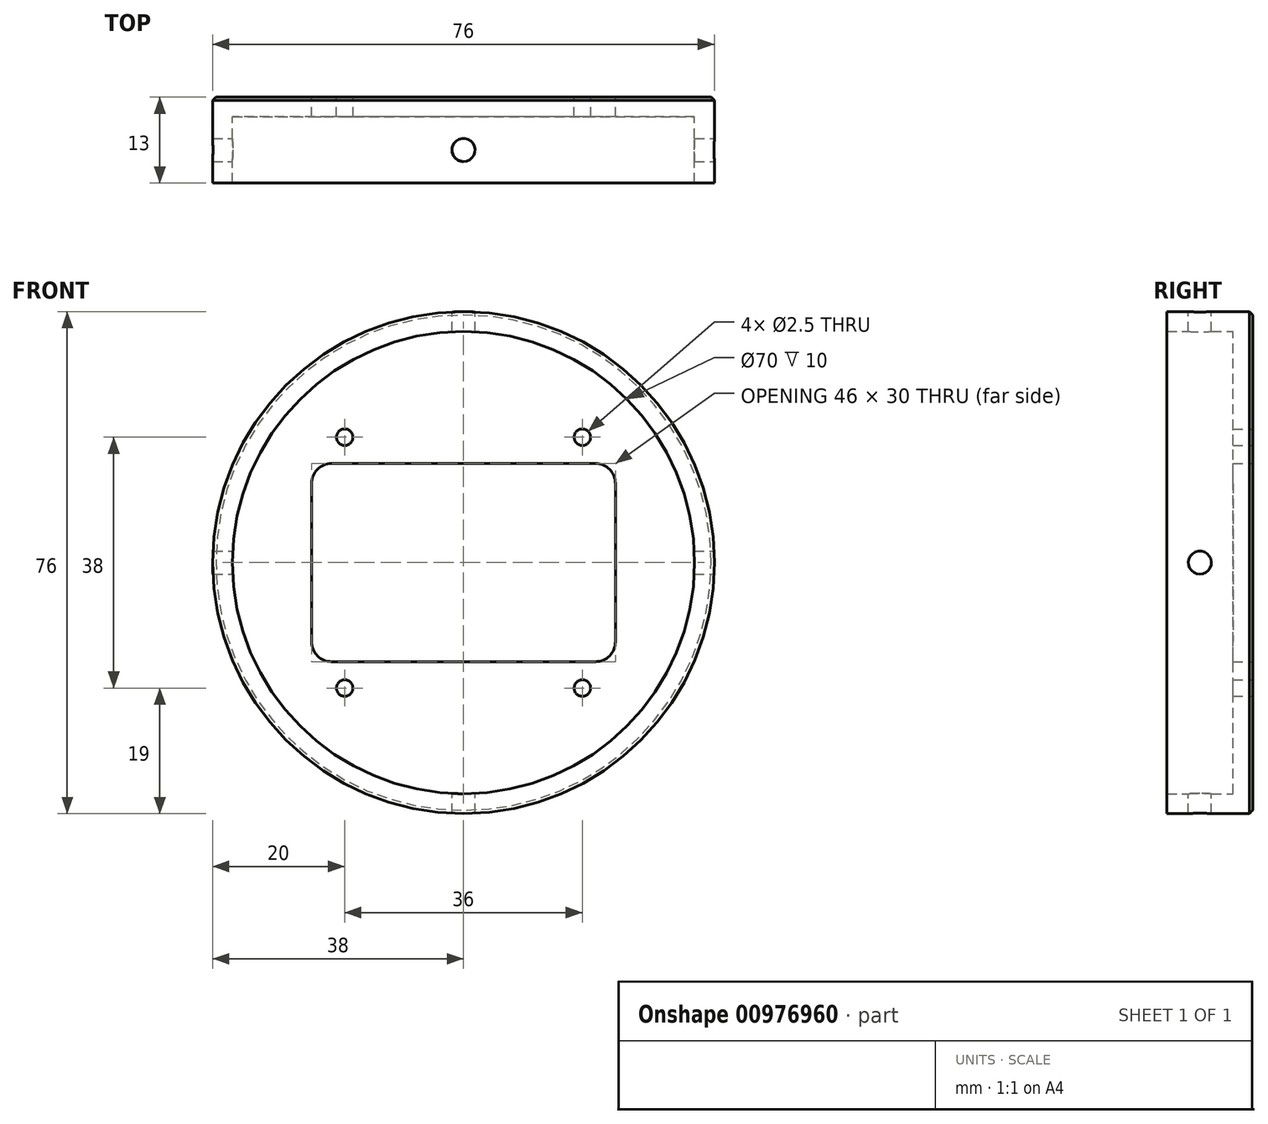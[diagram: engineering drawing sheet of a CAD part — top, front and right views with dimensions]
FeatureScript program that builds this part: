
annotation { "Feature Type Name" : "Feature", "Feature Type Description" : "" }
export const myFeature = defineFeature(function(context is Context, id is Id, definition is map)
    precondition{}
    {
        {
            var Q0;
            Q0=qCreatedBy(makeId("Front.planeOp"),FACE);
            var sketch = newSketch(context, id + "F0", { "sketchPlane" : qUnion([Q0])});
            skCircle(sketch, "E0", {"center": v(0, 0) * mm, "radius": 38 * mm});
            skSolve(sketch);
        }
        {
            var Q0;
            Q0=makeQuery(id+"F0.imprint","IMPRINT",FACE,{"disambiguationData":[TD([[makeQuery(id+"F0.imprint","IMPRINT",EDGE,{"derivedFrom":sQuery(id+"F0.wireOp",EDGE,"E0")}),1.0]])]});
            extrude(context, id + "F1", {"entities" : qUnion([Q0]), "depth" : 13 * mm, "offsetDistance" : 25 * mm});
        }
        {
            var Q0;
            Q0=makeQuery(id+"F1.opExtrude","CAP_FACE",FACE,{"disambiguationData":[OSD([sQuery(id+"F0.wireOp",EDGE,"E0")])],"isStart":false});
            shell(context, id + "F2", {"entities" : qUnion([Q0]), "thickness" : 3 * mm});
        }
        {
            var Q0;
            Q0=makeQuery(id+"F1.opExtrude","CAP_FACE",FACE,{"disambiguationData":[OSD([sQuery(id+"F0.wireOp",EDGE,"E0")])],"isStart":true});
            var sketch = newSketch(context, id + "F3", { "sketchPlane" : qUnion([Q0])});
            skPoint(sketch, "E1", {"position": v(-20, 12) * mm});
            skPoint(sketch, "E2", {"position": v(-20, -12) * mm});
            skPoint(sketch, "E3", {"position": v(20, -12) * mm});
            skPoint(sketch, "E4", {"position": v(20, 12) * mm});
            skArc(sketch, "E5", {"start": v(-20, 15) * mm, "mid": v(-22.12, 14.12) * mm, "end": v(-23, 12) * mm});
            skArc(sketch, "E6", {"start": v(-23, -12) * mm, "mid": v(-22.12, -14.12) * mm, "end": v(-20, -15) * mm});
            skArc(sketch, "E7", {"start": v(23, 12) * mm, "mid": v(22.12, 14.12) * mm, "end": v(20, 15) * mm});
            skArc(sketch, "E8", {"start": v(20, -15) * mm, "mid": v(22.12, -14.12) * mm, "end": v(23, -12) * mm});
            skLineSegment(sketch, "E9", {"start": v(-20, 15) * mm, "end": v(20, 15) * mm});
            skLineSegment(sketch, "E10", {"start": v(23, 12) * mm, "end": v(23, -12) * mm});
            skLineSegment(sketch, "E11", {"start": v(20, -15) * mm, "end": v(-20, -15) * mm});
            skLineSegment(sketch, "E12", {"start": v(-20, -12) * mm, "end": v(-23, -12) * mm});
            skLineSegment(sketch, "E13", {"start": v(-23, -12) * mm, "end": v(-23, 12) * mm});
            skSolve(sketch);
        }
        {
            var Q0;
            Q0=makeQuery(id+"F3.imprint","IMPRINT",FACE,{"disambiguationData":[TD([[makeQuery(id+"F3.imprint","IMPRINT",EDGE,{"derivedFrom":sQuery(id+"F3.wireOp",EDGE,"E5")}),1.0]])]});
            extrude(context, id + "F4", {"entities" : qUnion([Q0]), "operationType" : NewBodyOperationType.REMOVE, "oppositeDirection" : true, "depth" : 25 * mm, "offsetDistance" : 25 * mm});
        }
        {
            var Q0;
            Q0=makeQuery(id+"F1.opExtrude","CAP_FACE",FACE,{"disambiguationData":[OSD([sQuery(id+"F0.wireOp",EDGE,"E0")])],"isStart":true});
            var sketch = newSketch(context, id + "F5", { "sketchPlane" : qUnion([Q0])});
            skPoint(sketch, "E14", {"position": v(18, 19) * mm});
            skPoint(sketch, "E15", {"position": v(-18, 19) * mm});
            skPoint(sketch, "E16", {"position": v(-18, -19) * mm});
            skPoint(sketch, "E17", {"position": v(18, -19) * mm});
            skSolve(sketch);
        }
        {
            var Q0;
            Q0=sQuery(id+"F5.wireOp",VERTEX,"E14");
            var Q1;
            Q1=sQuery(id+"F5.wireOp",VERTEX,"E15");
            var Q2;
            Q2=sQuery(id+"F5.wireOp",VERTEX,"E16");
            var Q3;
            Q3=sQuery(id+"F5.wireOp",VERTEX,"E17");
            var Q4;
            Q4=makeQuery(id+"F1.opExtrude","SWEPT_BODY",BODY,{"disambiguationData":[OSD([sQuery(id+"F0.wireOp",EDGE,"E0")])]});
            hole(context, id + "F6", {"style" : HoleStyle.SIMPLE, "endStyle" : HoleEndStyle.THROUGH, "standardTappedOrClearance" : lookupTablePath({ "standard" : "ISO", "engagement" : "75%", "pitch" : "0.5 mm", "size" : "M3", "type" : "Tapped" }), "standardBlindInLast" : lookupTablePath({ "standard" : "ISO", "fit" : "Normal", "engagement" : "75%", "pitch" : "0.5 mm", "size" : "M3", "type" : "Clearance & tapped" }), "holeDiameter" : 2.5 * mm, "majorDiameter" : 3 * mm, "showTappedDepth" : true, "isTappedThrough" : true, "tappedDepth" : 12.6 * mm, "tapClearance" : 3, "startFromSketch" : true, "locations" : qUnion([Q0, Q1, Q2, Q3]), "scope" : qUnion([Q4])});
        }
        {
            var Q0;
            Q0=qCreatedBy(makeId("Right.planeOp"),FACE);
            cPlane(context, id + "F7", {"entities" : qUnion([Q0]), "cplaneType" : CPlaneType.OFFSET, "offset" : 38 * mm, "width" : 150 * mm, "height" : 150 * mm});
        }
        {
            var Q0;
            Q0=qCreatedBy(id+"F7.planeOp",FACE);
            var sketch = newSketch(context, id + "F8", { "sketchPlane" : qUnion([Q0])});
            skPoint(sketch, "E18", {"position": v(-8, 0) * mm});
            skSolve(sketch);
        }
        {
            var Q0;
            Q0=sQuery(id+"F8.wireOp",VERTEX,"E18");
            var Q1;
            Q1=makeQuery(id+"F1.opExtrude","SWEPT_BODY",BODY,{"disambiguationData":[OSD([sQuery(id+"F0.wireOp",EDGE,"E0")])]});
            hole(context, id + "F9", {"style" : HoleStyle.SIMPLE, "endStyle" : HoleEndStyle.THROUGH, "standardTappedOrClearance" : lookupTablePath({ "standard" : "ISO", "engagement" : "75%", "pitch" : "0.5 mm", "size" : "M4", "type" : "Tapped" }), "standardBlindInLast" : lookupTablePath({ "standard" : "ISO", "fit" : "Normal", "engagement" : "75%", "pitch" : "0.5 mm", "size" : "M4", "type" : "Clearance & tapped" }), "holeDiameter" : 3.5 * mm, "majorDiameter" : 4 * mm, "showTappedDepth" : true, "isTappedThrough" : true, "tappedDepth" : 12.6 * mm, "tapClearance" : 3, "startFromSketch" : true, "locations" : qUnion([Q0]), "scope" : qUnion([Q1])});
        }
        {
            var Q0;
            Q0=qCreatedBy(makeId("Top.planeOp"),FACE);
            cPlane(context, id + "F10", {"entities" : qUnion([Q0]), "cplaneType" : CPlaneType.OFFSET, "offset" : 38 * mm, "width" : 150 * mm, "height" : 150 * mm});
        }
        {
            var Q0;
            Q0=qCreatedBy(id+"F10.planeOp",FACE);
            var sketch = newSketch(context, id + "F11", { "sketchPlane" : qUnion([Q0])});
            skPoint(sketch, "E19", {"position": v(0, -8) * mm});
            skSolve(sketch);
        }
        {
            var Q0;
            Q0=sQuery(id+"F11.wireOp",VERTEX,"E19");
            var Q1;
            Q1=makeQuery(id+"F1.opExtrude","SWEPT_BODY",BODY,{"disambiguationData":[OSD([sQuery(id+"F0.wireOp",EDGE,"E0")])]});
            hole(context, id + "F12", {"style" : HoleStyle.SIMPLE, "endStyle" : HoleEndStyle.THROUGH, "standardTappedOrClearance" : lookupTablePath({ "standard" : "ISO", "engagement" : "75%", "pitch" : "0.5 mm", "size" : "M4", "type" : "Tapped" }), "standardBlindInLast" : lookupTablePath({ "standard" : "ISO", "fit" : "Normal", "engagement" : "75%", "pitch" : "0.5 mm", "size" : "M4", "type" : "Clearance & tapped" }), "holeDiameter" : 3.5 * mm, "majorDiameter" : 4 * mm, "showTappedDepth" : true, "isTappedThrough" : true, "tappedDepth" : 12.6 * mm, "tapClearance" : 3, "startFromSketch" : true, "locations" : qUnion([Q0]), "scope" : qUnion([Q1])});
        }
        {
            var Q0;
            Q0=makeQuery(id+"F1.opExtrude","CAP_EDGE",EDGE,{"disambiguationData":[OSD([sQuery(id+"F0.wireOp",EDGE,"E0")])],"isStart":true});
            chamfer(context, id + "F13", {"entities" : qUnion([Q0]), "width" : .5 * mm, "tangentPropagation" : true});
        }
    });
